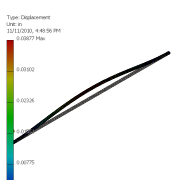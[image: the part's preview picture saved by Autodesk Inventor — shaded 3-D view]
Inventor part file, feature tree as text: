
AUTODESK INVENTOR PART (.ipt)
format: ipt  version: 2011 (Build 150239000, 239)  size: 351,744 bytes
history: native  units: in
note: dims shown in document units (in); Inventor stores cm internally (conversion verified against a paired STEP export)
features: extrude x1, sketch x1
ambient origin geometry x8: Origin, YZ Plane, XZ Plane, XY Plane, X Axis, Y Axis, Z Axis, Center Point
bodies: Solid1 (feature_tree)
feature tree (2):
  extrude  "Extrusion1"  Depth=120.0in TaperAngle=0.0deg
  sketch  "Sketch1"  dims[d0=1.2in d1=1.2in d2=0.475in d3=0.475in d4=0.3625in d5=0.3625in d6=0.3625in d7=0.085in d8=0.325in d9=0.4375in d10=0.325in d11=0.4375in d12=0.125in d13=0.125in d14=0.125in d15=0.125in d16=0.15in d17=0.15in d18=0.03in d19=0.03in d20=0.03in d21=0.15in d22=0.15in d23=0.03in d24=0.03in d25=0.275in d26=0.425in d27=0.075in d28=0.075in d29=0.425in d30=0.2125in d31=0.2125in d32=0.0375in d33=0.0375in d34=0.2125in d35=0.0375in d36=0.1in d37=0.05in d38=0.1in d39=0.05in d40=0.1in d41=0.0in d42=0.05in d43=0.1in d44=0.05in d45=0.025in d46=0.025in d47=0.025in d48=0.025in d49=0.025in d50=0.0in d51=0.0in d52=0.025in d53=0.0in d54=0.025in d55=0.0in d56=0.0in d57=0.0in d58=0.025in d59=0.0in d60=0.0in d61=120.0in d62=0.0in d63=1.2in]
